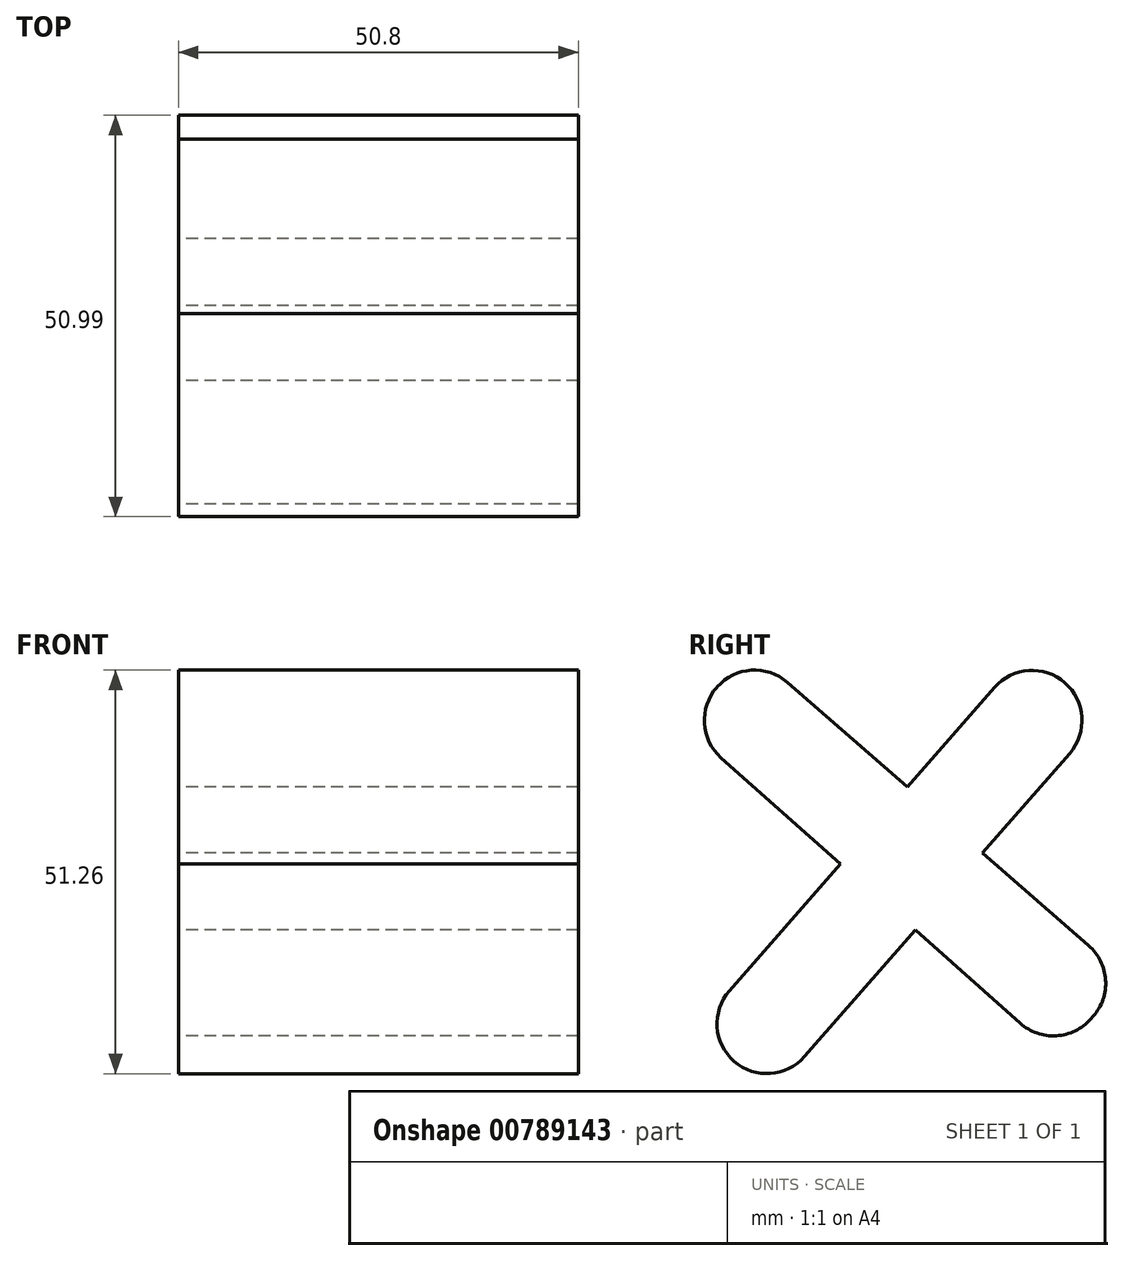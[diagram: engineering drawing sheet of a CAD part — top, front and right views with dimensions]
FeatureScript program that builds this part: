
annotation { "Feature Type Name" : "Feature", "Feature Type Description" : "" }
export const myFeature = defineFeature(function(context is Context, id is Id, definition is map)
    precondition{}
    {
        {
            var Q0;
            Q0=qCreatedBy(makeId("Right.planeOp"),FACE);
            var sketch = newSketch(context, id + "F0", { "sketchPlane" : qUnion([Q0])});
            skLineSegment(sketch, "E0", {"start": v(-23.48, 22.27) * mm, "end": v(-23.5, 22.23) * mm});
            skLineSegment(sketch, "E1", {"start": v(-22.98, 13.27) * mm, "end": v(-7.82, -0.19) * mm});
            skLineSegment(sketch, "E2", {"start": v(23.98, -19.92) * mm, "end": v(24.28, -19.59) * mm});
            skLineSegment(sketch, "E3", {"start": v(-14.55, 22.83) * mm, "end": v(0.67, 9.54) * mm});
            skLineSegment(sketch, "E4", {"start": v(-21.93, -16.33) * mm, "end": v(-7.82, -0.19) * mm});
            skLineSegment(sketch, "E5", {"start": v(20.7, 22.8) * mm, "end": v(20.7, 22.8) * mm});
            skLineSegment(sketch, "E6", {"start": v(21.3, 13.84) * mm, "end": v(10.24, 1.18) * mm});
            skLineSegment(sketch, "E7", {"start": v(-21.04, -25.52) * mm, "end": v(-21.04, -25.52) * mm});
            skLineSegment(sketch, "E8.trimOffspring", {"start": v(10.24, 1.18) * mm, "end": v(23.7, -10.59) * mm});
            skLineSegment(sketch, "E9.trimOffspring", {"start": v(0.67, 9.54) * mm, "end": v(11.74, 22.2) * mm});
            skLineSegment(sketch, "E10.trimOffspring", {"start": v(1.68, -8.62) * mm, "end": v(15.01, -20.46) * mm});
            skLineSegment(sketch, "E11.trimOffspring", {"start": v(1.68, -8.62) * mm, "end": v(-12.36, -24.68) * mm});
            skPoint(sketch, "E12.visualSharp", {"position": v(-16.3, -29.2) * mm});
            skArc(sketch, "E12.filletArc", {"start": v(-21.04, -25.52) * mm, "mid": v(-16.53, -26.83) * mm, "end": v(-12.36, -24.68) * mm});
            skPoint(sketch, "E13.visualSharp", {"position": v(-26.36, -21.4) * mm});
            skArc(sketch, "E13.filletArc", {"start": v(-21.93, -16.33) * mm, "mid": v(-23.46, -21.12) * mm, "end": v(-21.04, -25.52) * mm});
            skPoint(sketch, "E14.visualSharp", {"position": v(19.76, -24.67) * mm});
            skArc(sketch, "E14.filletArc", {"start": v(15.01, -20.46) * mm, "mid": v(19.6, -22.05) * mm, "end": v(23.98, -19.92) * mm});
            skPoint(sketch, "E15.visualSharp", {"position": v(28.52, -14.8) * mm});
            skArc(sketch, "E15.filletArc", {"start": v(24.28, -19.59) * mm, "mid": v(25.86, -14.97) * mm, "end": v(23.7, -10.59) * mm});
            skPoint(sketch, "E16.visualSharp", {"position": v(25.48, 18.62) * mm});
            skArc(sketch, "E16.filletArc", {"start": v(21.3, 13.84) * mm, "mid": v(22.85, 18.45) * mm, "end": v(20.7, 22.8) * mm});
            skPoint(sketch, "E17.visualSharp", {"position": v(15.91, 26.98) * mm});
            skArc(sketch, "E17.filletArc", {"start": v(20.7, 22.8) * mm, "mid": v(16.1, 24.36) * mm, "end": v(11.74, 22.2) * mm});
            skPoint(sketch, "E18.visualSharp", {"position": v(-19.3, 26.98) * mm});
            skArc(sketch, "E18.filletArc", {"start": v(-14.55, 22.83) * mm, "mid": v(-19.13, 24.39) * mm, "end": v(-23.48, 22.27) * mm});
            skPoint(sketch, "E19.visualSharp", {"position": v(-27.73, 17.48) * mm});
            skArc(sketch, "E19.filletArc", {"start": v(-23.5, 22.23) * mm, "mid": v(-25.1, 17.64) * mm, "end": v(-22.98, 13.27) * mm});
            skSolve(sketch);
        }
        {
            var Q0;
            Q0 = qSketchRegion(id + "F0", true);
            extrude(context, id + "F1", {"entities" : qUnion([Q0]), "depth" : 25.4 * mm, "offsetDistance" : 25.4 * mm, "hasSecondDirection" : true, "secondDirectionOppositeDirection" : true, "secondDirectionDepth" : 25.4 * mm});
        }
    });
